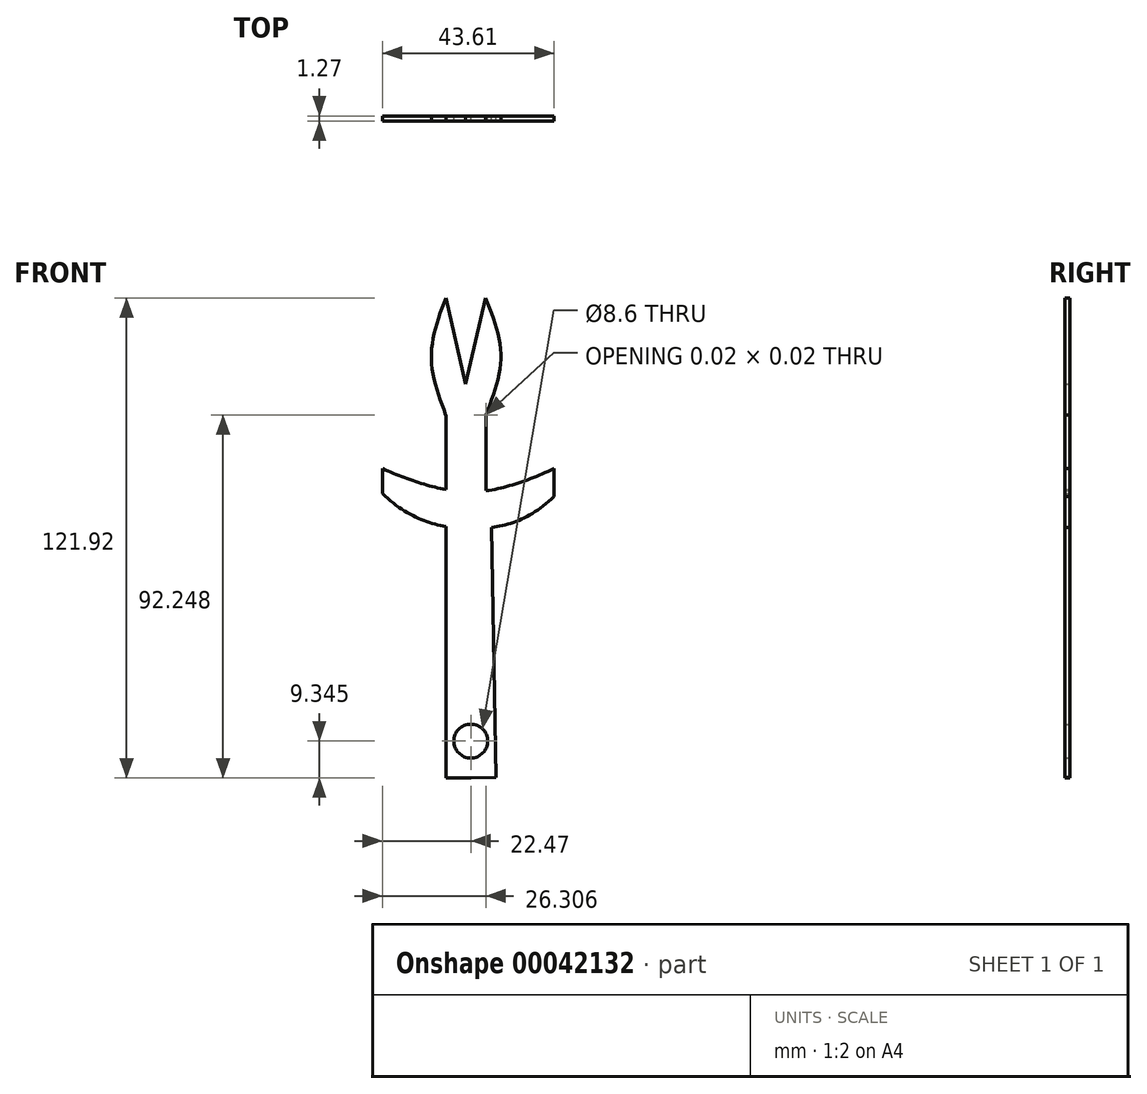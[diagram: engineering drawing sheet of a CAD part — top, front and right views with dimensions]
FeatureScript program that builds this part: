
annotation { "Feature Type Name" : "Feature", "Feature Type Description" : "" }
export const myFeature = defineFeature(function(context is Context, id is Id, definition is map)
    precondition{}
    {
        {
            var Q0;
            Q0=qCreatedBy(makeId("Front.planeOp"),FACE);
            var sketch = newSketch(context, id + "F0", { "sketchPlane" : qUnion([Q0])});
            skLineSegment(sketch, "E0", {"start": v(0, 0) * mm, "end": v(-6.35, 0) * mm});
            skLineSegment(sketch, "E1", {"start": v(0, 0) * mm, "end": v(6.35, 0.1) * mm});
            skFitSpline(sketch, "E2", {"points": [v(-22.47, 72.22) * mm, v(0, 63.3) * mm, v(21.14, 71.52) * mm], "startDerivative": vector(44.65, -42.56) * mm, "endDerivative": vector(42.56, 41.57) * mm});
            skLineSegment(sketch, "E3", {"start": v(-22.47, 72.22) * mm, "end": v(-22.47, 78.57) * mm});
            skLineSegment(sketch, "E4", {"start": v(21.14, 71.52) * mm, "end": v(21.14, 78.57) * mm});
            skFitSpline(sketch, "E5", {"points": [v(-22.47, 78.57) * mm, v(0, 72.7) * mm, v(21.14, 78.57) * mm], "startDerivative": vector(44.68, -19.03) * mm, "endDerivative": vector(42.53, 19.2) * mm});
            skPoint(sketch, "E6.end.orphan", {"position": v(17.01, 87.66) * mm});
            skPoint(sketch, "E7.start.orphan", {"position": v(12.12, 63.3) * mm});
            skPoint(sketch, "E8.start.orphan", {"position": v(-12.7, 63.3) * mm});
            skLineSegment(sketch, "E9", {"start": v(-6.35, 0) * mm, "end": v(-6.35, 63.83) * mm});
            skLineSegment(sketch, "E10", {"start": v(6.35, 0.1) * mm, "end": v(5.27, 63.6) * mm});
            skPoint(sketch, "E11.end.orphan", {"position": v(-6.75, 87.66) * mm});
            skLineSegment(sketch, "E12", {"start": v(-6.35, 92.26) * mm, "end": v(-6.35, 73.27) * mm});
            skPoint(sketch, "E13.orphan", {"position": v(0, 100.12) * mm});
            skPoint(sketch, "E14.orphan", {"position": v(5.27, 121.92) * mm});
            skPoint(sketch, "E15.1.internal.orphan", {"position": v(0, 137.97) * mm});
            skPoint(sketch, "E15.endDerivative.orphan", {"position": v(5.27, 97.92) * mm});
            skPoint(sketch, "E15.startDerivative.orphan", {"position": v(0, 121.92) * mm});
            skLineSegment(sketch, "E16", {"start": v(3.84, 92.26) * mm, "end": v(3.83, 92.26) * mm});
            skLineSegment(sketch, "E17", {"start": v(3.83, 92.26) * mm, "end": v(3.83, 72.96) * mm});
            skPoint(sketch, "E18.orphan", {"position": v(0, 92.26) * mm});
            skCircle(sketch, "E19", {"center": v(0, 9.34) * mm, "radius": 4.3 * mm});
            skLineSegment(sketch, "E20", {"start": v(-6.35, 92.26) * mm, "end": v(-6.38, 92.26) * mm});
            skPoint(sketch, "E21.start.orphan", {"position": v(-6.35, 121.92) * mm});
            skEllipticalArc(sketch, "E22", {});
            skPoint(sketch, "E23.orphan", {"position": v(-1.28, 121.92) * mm});
            skPoint(sketch, "E24.start.orphan", {"position": v(-1.26, 92.26) * mm});
            skPoint(sketch, "E25.orphan", {"position": v(7.65, 92.26) * mm});
            skLineSegment(sketch, "E26", {"start": v(-6.35, 92.22) * mm, "end": v(3.84, 92.22) * mm});
            skEllipticalArc(sketch, "E27.trimOffspring", {});
            skPoint(sketch, "E28.1.internal.orphan", {"position": v(10.56, 107.1) * mm});
            skPoint(sketch, "E28.end.orphan", {"position": v(7.65, 121.92) * mm});
            skLineSegment(sketch, "E29", {"start": v(-6.9, 121.92) * mm, "end": v(-6.9, 121.92) * mm});
            skPoint(sketch, "E30.1.internal.orphan", {"position": v(-10.16, 112.43) * mm});
            skPoint(sketch, "E31.start.orphan", {"position": v(-6.9, 100.12) * mm});
            skPoint(sketch, "E32.1.internal.orphan", {"position": v(-6.9, 112.43) * mm});
            skPoint(sketch, "E33.1.internal.orphan", {"position": v(-4.08, 112.43) * mm});
            skPoint(sketch, "E34.start.orphan", {"position": v(5.27, 100.12) * mm});
            skPoint(sketch, "E35.end.orphan", {"position": v(-1.26, 121.92) * mm});
            skPoint(sketch, "E36.end.orphan", {"position": v(-1.25, 92.22) * mm});
            skPoint(sketch, "E37.end.orphan", {"position": v(-12.55, 100.12) * mm});
            skPoint(sketch, "E38.start.orphan", {"position": v(-1.26, 100.12) * mm});
            skPoint(sketch, "E39.orphan", {"position": v(9.9, 100.12) * mm});
            skPoint(sketch, "E40.1.internal.orphan", {"position": v(-8.52, 112.43) * mm});
            skPoint(sketch, "E41.1.internal.orphan", {"position": v(1.57, 112.43) * mm});
            skPoint(sketch, "E42.1.internal.orphan", {"position": v(6.38, 112.43) * mm});
            skPoint(sketch, "E42.end.orphan", {"position": v(4.32, 100.12) * mm});
            skPoint(sketch, "E43.1.internal.orphan", {"position": v(-13.31, 107.1) * mm});
            skPoint(sketch, "E43.2.internal.orphan", {"position": v(-10.16, 121.92) * mm});
            skPoint(sketch, "E44.end.orphan", {"position": v(7.65, 92.22) * mm});
            skPoint(sketch, "E45.orphan", {"position": v(-0.63, 100.12) * mm});
            skPoint(sketch, "E46.1.internal.orphan", {"position": v(-10.03, 107.1) * mm});
            skPoint(sketch, "E47.end.orphan", {"position": v(-1.27, 100.12) * mm});
            skPoint(sketch, "E48.1.internal.orphan", {"position": v(7.65, 107.1) * mm});
            skLineSegment(sketch, "E49", {"start": v(-6.35, 92.26) * mm, "end": v(-6.35, 92.22) * mm});
            skLineSegment(sketch, "E50", {"start": v(-6.35, 121.92) * mm, "end": v(-1.28, 100.12) * mm});
            skLineSegment(sketch, "E51", {"start": v(-1.28, 100.12) * mm, "end": v(3.8, 121.92) * mm});
            skFitSpline(sketch, "E52", {"points": [v(-6.35, 121.92) * mm, v(-10.03, 107.1) * mm, v(-6.38, 92.26) * mm], "startDerivative": vector(-11.01, -29.66) * mm, "endDerivative": vector(10.94, -29.67) * mm});
            skLineSegment(sketch, "E53", {"start": v(3.84, 92.26) * mm, "end": v(3.84, 92.22) * mm});
            skFitSpline(sketch, "E54", {"points": [v(3.8, 121.92) * mm, v(7.65, 107.1) * mm, v(3.84, 92.22) * mm], "startDerivative": vector(11.54, -29.66) * mm, "endDerivative": vector(-11.45, -29.75) * mm});
            const initialGuessF0  = {"E22": [-0.00127, 0.10709014901935063, 0, -1, 0.017645876799215893, 0.009439947865050294, 5.710609058103408, 5.714958242728358], "E27.trimOffspring": [-0.00127, 0.10709014901935063, 0, -1, 0.017645876799215893, 0.009439947865050294, 0.5682270644512292, 0.572576249076178]};
            skSetInitialGuess(sketch, initialGuessF0);
            skSolve(sketch);
        }
        {
            var Q0;
            Q0=qSketchRegion(id+"F0",true);
            extrude(context, id + "F1", {"entities" : qUnion([Q0]), "depth" : 1.27 * mm});
        }
    });
